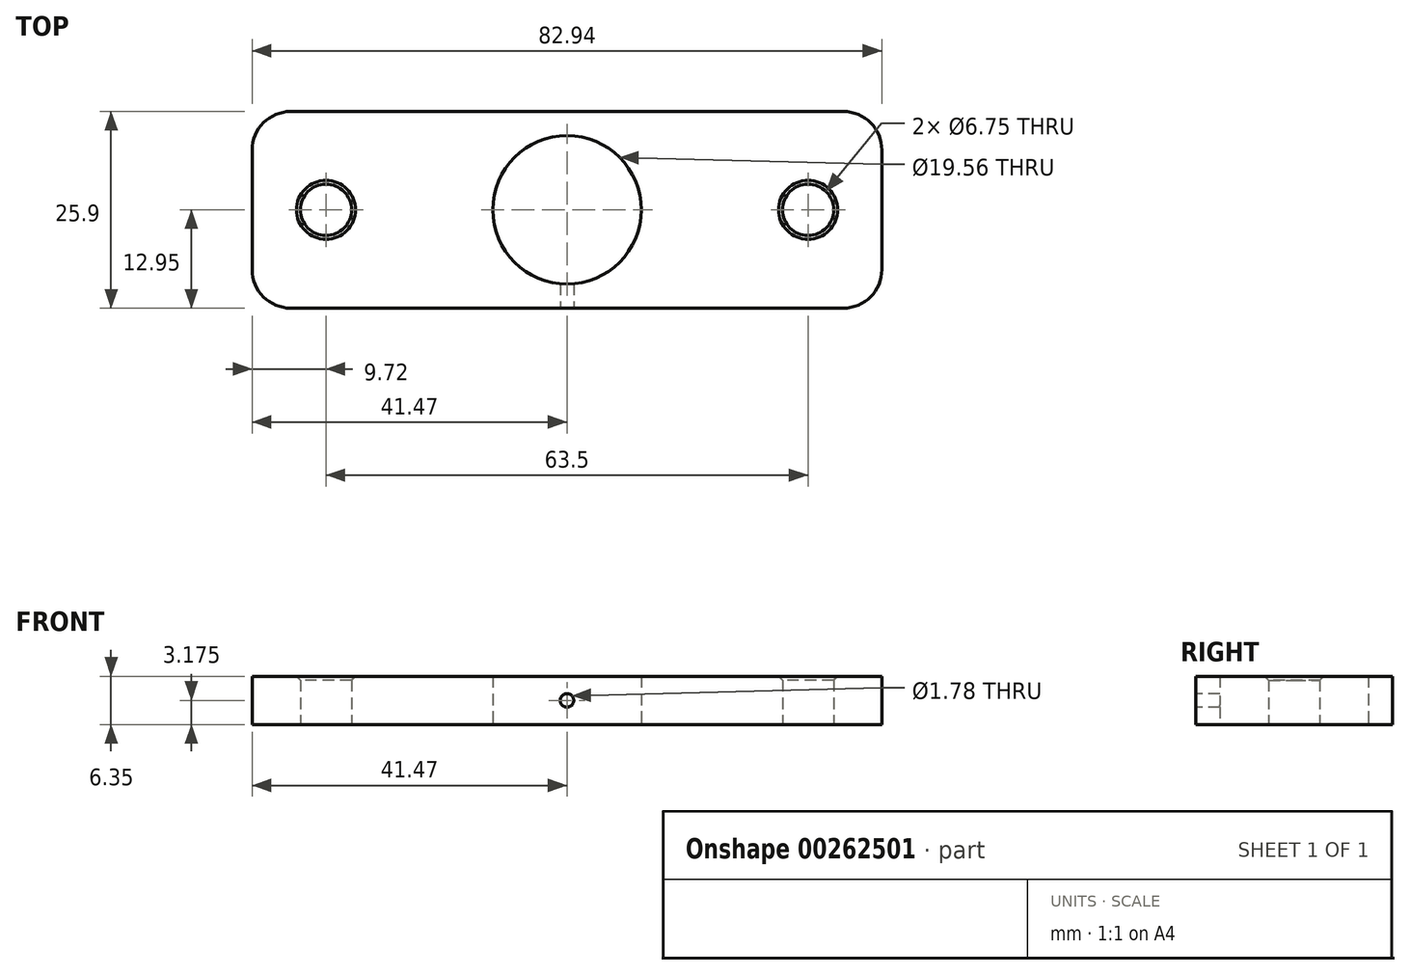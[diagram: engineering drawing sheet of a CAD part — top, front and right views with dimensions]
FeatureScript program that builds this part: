
annotation { "Feature Type Name" : "Feature", "Feature Type Description" : "" }
export const myFeature = defineFeature(function(context is Context, id is Id, definition is map)
    precondition{}
    {
        {
            var Q0;
            Q0=qCreatedBy(makeId("Top.planeOp"),FACE);
            var sketch = newSketch(context, id + "F0", { "sketchPlane" : qUnion([Q0])});
            skLineSegment(sketch, "E0.bottom", {"start": v(41.47, -12.95) * mm, "end": v(-41.47, -12.95) * mm});
            skLineSegment(sketch, "E0.top", {"start": v(41.47, 12.95) * mm, "end": v(-41.47, 12.95) * mm});
            skLineSegment(sketch, "E0.left", {"start": v(41.47, -12.95) * mm, "end": v(41.47, 12.95) * mm});
            skLineSegment(sketch, "E0.right", {"start": v(-41.47, -12.95) * mm, "end": v(-41.47, 12.95) * mm});
            skPoint(sketch, "E0.middle", {"position": v(0, 0) * mm});
            skCircle(sketch, "E1", {"center": v(0, 0) * mm, "radius": 9.78 * mm});
            skCircle(sketch, "E2", {"center": v(31.75, 0) * mm, "radius": 3.37 * mm});
            skCircle(sketch, "E3", {"center": v(-31.75, 0) * mm, "radius": 3.37 * mm});
            skSolve(sketch);
        }
        {
            var Q0;
            Q0=makeQuery(id+"F0.imprint","IMPRINT",FACE,{"disambiguationData":[TD([[makeQuery(id+"F0.imprint","IMPRINT",EDGE,{"derivedFrom":sQuery(id+"F0.wireOp",EDGE,"E0.bottom")}),-1.0]])]});
            extrude(context, id + "F1", {"entities" : qUnion([Q0]), "depth" : 6.35 * mm});
        }
        {
            var Q0;
            Q0=makeQuery(id+"F1.opExtrude","SWEPT_FACE",FACE,{"disambiguationData":[OSD([sQuery(id+"F0.wireOp",EDGE,"E0.bottom")])]});
            var sketch = newSketch(context, id + "F2", { "sketchPlane" : qUnion([Q0])});
            skCircle(sketch, "E4", {"center": v(0, 3.18) * mm, "radius": 0.89 * mm});
            skLineSegment(sketch, "E5", {"start": v(0, 0) * mm, "end": v(0, 3.18) * mm, "construction": true});
            skLineSegment(sketch, "E6", {"start": v(0, 6.35) * mm, "end": v(0, 3.18) * mm, "construction": true});
            skSolve(sketch);
        }
        {
            var Q0;
            Q0 = qSketchRegion(id + "F2", true);
            extrude(context, id + "F3", {"entities" : qUnion([Q0]), "operationType" : NewBodyOperationType.REMOVE, "endBound" : BoundingType.UP_TO_NEXT, "oppositeDirection" : true, "depth" : 25.4 * mm});
        }
        {
            var Q0;
            Q0=makeQuery(id+"F1.opExtrude","SWEPT_EDGE",EDGE,{"disambiguationData":[OSD([sQuery(id+"F0.wireOp",EDGE,"E0.bottom"),sQuery(id+"F0.wireOp",EDGE,"E0.left")])]});
            var Q1;
            Q1=makeQuery(id+"F1.opExtrude","SWEPT_EDGE",EDGE,{"disambiguationData":[OSD([sQuery(id+"F0.wireOp",EDGE,"E0.top"),sQuery(id+"F0.wireOp",EDGE,"E0.left")])]});
            var Q2;
            Q2=makeQuery(id+"F1.opExtrude","SWEPT_EDGE",EDGE,{"disambiguationData":[OSD([sQuery(id+"F0.wireOp",EDGE,"E0.bottom"),sQuery(id+"F0.wireOp",EDGE,"E0.right")])]});
            var Q3;
            Q3=makeQuery(id+"F1.opExtrude","SWEPT_EDGE",EDGE,{"disambiguationData":[OSD([sQuery(id+"F0.wireOp",EDGE,"E0.top"),sQuery(id+"F0.wireOp",EDGE,"E0.right")])]});
            fillet(context, id + "F4", {"entities" : qUnion([Q0, Q1, Q2, Q3]), "radius" : 5.08 * mm, "tangentPropagation" : true, "allowEdgeOverflow" : false});
        }
        {
            var Q0;
            Q0=makeQuery(id+"F1.opExtrude","CAP_EDGE",EDGE,{"disambiguationData":[OSD([sQuery(id+"F0.wireOp",EDGE,"E3")])],"isStart":false});
            var Q1;
            Q1=makeQuery(id+"F1.opExtrude","CAP_EDGE",EDGE,{"disambiguationData":[OSD([sQuery(id+"F0.wireOp",EDGE,"E2")])],"isStart":false});
            chamfer(context, id + "F5", {"entities" : qUnion([Q0, Q1]), "width" : 0.5 * mm, "tangentPropagation" : true});
        }
    });
